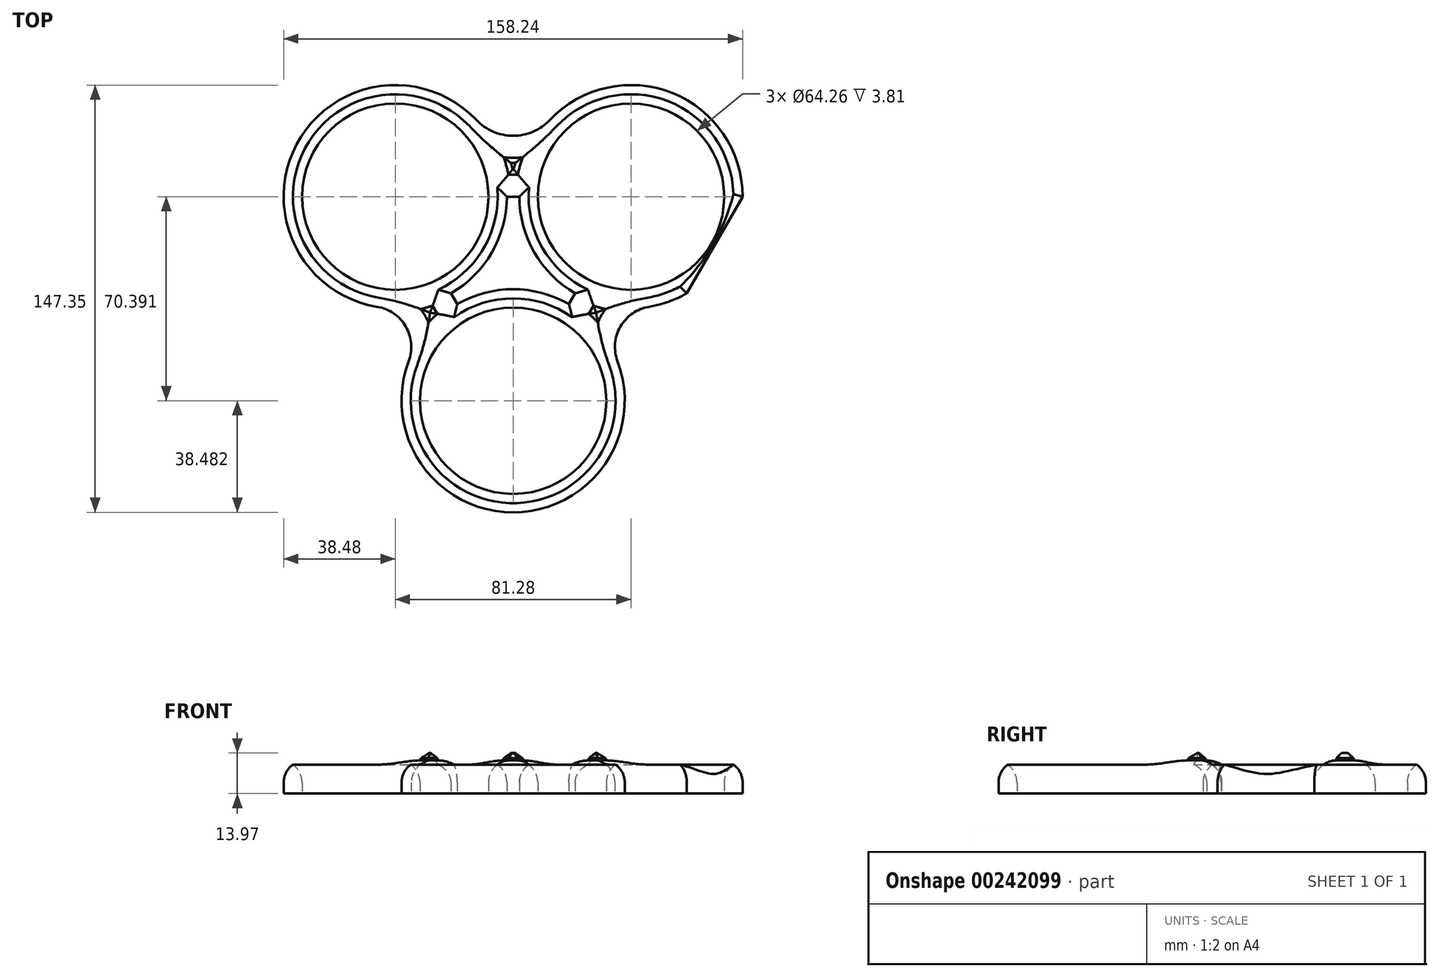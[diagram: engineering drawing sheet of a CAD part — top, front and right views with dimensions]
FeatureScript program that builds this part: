
annotation { "Feature Type Name" : "Feature", "Feature Type Description" : "" }
export const myFeature = defineFeature(function(context is Context, id is Id, definition is map)
    precondition{}
    {
        {
            var Q0;
            Q0=qCreatedBy(makeId("Top.planeOp"),FACE);
            var sketch = newSketch(context, id + "F0", { "sketchPlane" : qUnion([Q0])});
            skCircle(sketch, "E0", {"center": v(-40.64, 29.67) * mm, "radius": 32.13 * mm});
            skCircle(sketch, "E1", {"center": v(40.64, 29.67) * mm, "radius": 32.13 * mm});
            skCircle(sketch, "E2", {"center": v(0, -40.72) * mm, "radius": 32.13 * mm});
            skCircle(sketch, "E3", {"center": v(0, 0) * mm, "radius": 114.2 * mm});
            skCircle(sketch, "E4.0", {"center": v(-40.64, 29.67) * mm, "radius": 38.48 * mm});
            skCircle(sketch, "E5.0", {"center": v(40.64, 29.67) * mm, "radius": 38.48 * mm});
            skCircle(sketch, "E6.0", {"center": v(0, -40.72) * mm, "radius": 38.48 * mm});
            skLineSegment(sketch, "E7", {"start": v(-60.1, 96.9) * mm, "end": v(60.55, 96.9) * mm});
            skLineSegment(sketch, "E8", {"start": v(-79.12, 29.67) * mm, "end": v(-38.48, -40.72) * mm});
            skLineSegment(sketch, "E9", {"start": v(38.48, -40.72) * mm, "end": v(79.12, 29.67) * mm});
            skLineSegment(sketch, "E10", {"start": v(-40.64, 68.15) * mm, "end": v(40.64, 68.15) * mm});
            skLineSegment(sketch, "E11", {"start": v(-40.64, 29.67) * mm, "end": v(40.64, 29.67) * mm});
            skLineSegment(sketch, "E12", {"start": v(40.64, 29.67) * mm, "end": v(0, -40.72) * mm});
            skLineSegment(sketch, "E13", {"start": v(-40.64, 29.67) * mm, "end": v(0, -40.72) * mm});
            skLineSegment(sketch, "E14", {"start": v(-20.32, -5.52) * mm, "end": v(-49.18, -22.19) * mm});
            skLineSegment(sketch, "E15", {"start": v(20.32, -5.52) * mm, "end": v(49.18, -22.19) * mm});
            skLineSegment(sketch, "E16", {"start": v(0, 29.67) * mm, "end": v(0, 68.15) * mm});
            skCircle(sketch, "E17", {"center": v(49.18, -22.19) * mm, "radius": 14.08 * mm});
            skCircle(sketch, "E18", {"center": v(-49.18, -22.19) * mm, "radius": 14.08 * mm});
            skCircle(sketch, "E19", {"center": v(0, 68.15) * mm, "radius": 17.49 * mm});
            skSolve(sketch);
        }
        {
            var Q0;
            {var subQ5=sQuery(id+"F0.wireOp",EDGE,"E0");var subQ9=sQuery(id+"F0.wireOp",EDGE,"E11");var subQ11=makeQuery(id+"F0.imprint","INTERSECT",VERTEX,{"derivedFrom":[subQ5,subQ9]});Q0=makeQuery(id+"F0.imprint","IMPRINT",FACE,{"disambiguationData":[TD([[makeQuery(id+"F0.imprint","IMPRINT",EDGE,{"disambiguationData":[TD([[subQ11,-1.0]])],"derivedFrom":subQ5}),-1.0]])]});}
            var Q1;
            {var subQ8=sQuery(id+"F0.wireOp",EDGE,"E11");var subQ9=sQuery(id+"F0.wireOp",EDGE,"E1");var subQ10=makeQuery(id+"F0.imprint","INTERSECT",VERTEX,{"derivedFrom":[subQ9,subQ8]});Q1=makeQuery(id+"F0.imprint","IMPRINT",FACE,{"disambiguationData":[TD([[makeQuery(id+"F0.imprint","IMPRINT",EDGE,{"disambiguationData":[TD([[subQ10,1.0]])],"derivedFrom":subQ9}),-1.0]])]});}
            var Q2;
            {var subQ5=sQuery(id+"F0.wireOp",EDGE,"E12");var subQ8=sQuery(id+"F0.wireOp",EDGE,"E2");var subQ9=makeQuery(id+"F0.imprint","INTERSECT",VERTEX,{"derivedFrom":[subQ8,subQ5]});Q2=makeQuery(id+"F0.imprint","IMPRINT",FACE,{"disambiguationData":[TD([[makeQuery(id+"F0.imprint","IMPRINT",EDGE,{"disambiguationData":[TD([[subQ9,1.0]])],"derivedFrom":subQ8}),-1.0]])]});}
            var Q3;
            {var subQ0=sQuery(id+"F0.wireOp",EDGE,"E17");var subQ1=sQuery(id+"F0.wireOp",EDGE,"E6.0");var subQ2=makeQuery(id+"F0.imprint","INTERSECT",VERTEX,{"derivedFrom":[subQ1,subQ0]});Q3=makeQuery(id+"F0.imprint","IMPRINT",FACE,{"disambiguationData":[TD([[makeQuery(id+"F0.imprint","IMPRINT",EDGE,{"disambiguationData":[TD([[subQ2,-1.0]])],"derivedFrom":subQ1}),-1.0]])]});}
            var Q4;
            {var subQ0=sQuery(id+"F0.wireOp",EDGE,"E12");var subQ1=sQuery(id+"F0.wireOp",EDGE,"E5.0");var subQ2=makeQuery(id+"F0.imprint","INTERSECT",VERTEX,{"derivedFrom":[subQ1,subQ0]});Q4=makeQuery(id+"F0.imprint","IMPRINT",FACE,{"disambiguationData":[TD([[makeQuery(id+"F0.imprint","IMPRINT",EDGE,{"disambiguationData":[TD([[subQ2,-1.0]])],"derivedFrom":subQ1}),-1.0]])]});}
            var Q5;
            {var subQ0=sQuery(id+"F0.wireOp",EDGE,"E13");var subQ1=sQuery(id+"F0.wireOp",EDGE,"E6.0");var subQ2=makeQuery(id+"F0.imprint","INTERSECT",VERTEX,{"derivedFrom":[subQ1,subQ0]});Q5=makeQuery(id+"F0.imprint","IMPRINT",FACE,{"disambiguationData":[TD([[makeQuery(id+"F0.imprint","IMPRINT",EDGE,{"disambiguationData":[TD([[subQ2,-1.0]])],"derivedFrom":subQ1}),-1.0]])]});}
            var Q6;
            {var subQ0=sQuery(id+"F0.wireOp",EDGE,"E18");var subQ1=sQuery(id+"F0.wireOp",EDGE,"E4.0");var subQ2=makeQuery(id+"F0.imprint","INTERSECT",VERTEX,{"derivedFrom":[subQ1,subQ0]});Q6=makeQuery(id+"F0.imprint","IMPRINT",FACE,{"disambiguationData":[TD([[makeQuery(id+"F0.imprint","IMPRINT",EDGE,{"disambiguationData":[TD([[subQ2,-1.0]])],"derivedFrom":subQ1}),-1.0]])]});}
            var Q7;
            {var subQ0=sQuery(id+"F0.wireOp",EDGE,"E19");var subQ1=sQuery(id+"F0.wireOp",EDGE,"E4.0");var subQ2=makeQuery(id+"F0.imprint","INTERSECT",VERTEX,{"derivedFrom":[subQ1,subQ0]});Q7=makeQuery(id+"F0.imprint","IMPRINT",FACE,{"disambiguationData":[TD([[makeQuery(id+"F0.imprint","IMPRINT",EDGE,{"disambiguationData":[TD([[subQ2,1.0]])],"derivedFrom":subQ1}),-1.0]])]});}
            var Q8;
            {var subQ0=sQuery(id+"F0.wireOp",EDGE,"E19");var subQ1=sQuery(id+"F0.wireOp",EDGE,"E5.0");var subQ2=makeQuery(id+"F0.imprint","INTERSECT",VERTEX,{"derivedFrom":[subQ1,subQ0]});Q8=makeQuery(id+"F0.imprint","IMPRINT",FACE,{"disambiguationData":[TD([[makeQuery(id+"F0.imprint","IMPRINT",EDGE,{"disambiguationData":[TD([[subQ2,-1.0]])],"derivedFrom":subQ1}),-1.0]])]});}
            var Q9;
            {var subQ0=sQuery(id+"F0.wireOp",EDGE,"E11");var subQ1=sQuery(id+"F0.wireOp",EDGE,"E0");var subQ2=makeQuery(id+"F0.imprint","INTERSECT",VERTEX,{"derivedFrom":[subQ1,subQ0]});Q9=makeQuery(id+"F0.imprint","IMPRINT",FACE,{"disambiguationData":[TD([[makeQuery(id+"F0.imprint","IMPRINT",EDGE,{"disambiguationData":[TD([[subQ2,1.0]])],"derivedFrom":subQ1}),-1.0]])]});}
            var Q10;
            {var subQ0=sQuery(id+"F0.wireOp",EDGE,"E11");var subQ1=sQuery(id+"F0.wireOp",EDGE,"E1");var subQ2=makeQuery(id+"F0.imprint","INTERSECT",VERTEX,{"derivedFrom":[subQ1,subQ0]});Q10=makeQuery(id+"F0.imprint","IMPRINT",FACE,{"disambiguationData":[TD([[makeQuery(id+"F0.imprint","IMPRINT",EDGE,{"disambiguationData":[TD([[subQ2,-1.0]])],"derivedFrom":subQ1}),-1.0]])]});}
            var Q11;
            {var subQ0=sQuery(id+"F0.wireOp",EDGE,"E12");var subQ1=sQuery(id+"F0.wireOp",EDGE,"E2");var subQ2=makeQuery(id+"F0.imprint","INTERSECT",VERTEX,{"derivedFrom":[subQ1,subQ0]});Q11=makeQuery(id+"F0.imprint","IMPRINT",FACE,{"disambiguationData":[TD([[makeQuery(id+"F0.imprint","IMPRINT",EDGE,{"disambiguationData":[TD([[subQ2,-1.0]])],"derivedFrom":subQ1}),-1.0]])]});}
            var Q12;
            {var subQ0=sQuery(id+"F0.wireOp",EDGE,"E8");var subQ1=sQuery(id+"F0.wireOp",EDGE,"E4.0");var subQ2=makeQuery(id+"F0.imprint","INTERSECT",VERTEX,{"disambiguationData":[OD(0.0)],"derivedFrom":[subQ1,subQ0]});Q12=makeQuery(id+"F0.imprint","IMPRINT",FACE,{"disambiguationData":[TD([[makeQuery(id+"F0.imprint","IMPRINT",EDGE,{"disambiguationData":[TD([[subQ2,-1.0]])],"derivedFrom":subQ1}),1.0]])]});}
            var Q13;
            {var subQ0=sQuery(id+"F0.wireOp",EDGE,"E9");var subQ1=sQuery(id+"F0.wireOp",EDGE,"E5.0");var subQ2=makeQuery(id+"F0.imprint","INTERSECT",VERTEX,{"disambiguationData":[OD(0.0)],"derivedFrom":[subQ1,subQ0]});Q13=makeQuery(id+"F0.imprint","IMPRINT",FACE,{"disambiguationData":[TD([[makeQuery(id+"F0.imprint","IMPRINT",EDGE,{"disambiguationData":[TD([[subQ2,1.0]])],"derivedFrom":subQ1}),1.0]])]});}
            extrude(context, id + "F1", {"entities" : qUnion([Q0, Q1, Q2, Q3, Q4, Q5, Q6, Q7, Q8, Q9, Q10, Q11, Q12, Q13]), "depth" : 11.43 * mm});
        }
        {
            var Q0;
            Q0=makeQuery(id+"F1.opExtrude","CAP_FACE",FACE,{"disambiguationData":[OSD([sQuery(id+"F0.wireOp",EDGE,"E0"),sQuery(id+"F0.wireOp",EDGE,"E1"),sQuery(id+"F0.wireOp",EDGE,"E2"),sQuery(id+"F0.wireOp",EDGE,"E4.0"),sQuery(id+"F0.wireOp",EDGE,"E5.0"),sQuery(id+"F0.wireOp",EDGE,"E6.0"),sQuery(id+"F0.wireOp",EDGE,"E11"),sQuery(id+"F0.wireOp",EDGE,"E12"),sQuery(id+"F0.wireOp",EDGE,"E13"),sQuery(id+"F0.wireOp",EDGE,"E17"),sQuery(id+"F0.wireOp",EDGE,"E18"),sQuery(id+"F0.wireOp",EDGE,"E19")])],"isStart":false});
            fillet(context, id + "F2", {"entities" : qUnion([Q0]), "radius" : 7.62 * mm, "tangentPropagation" : true, "allowEdgeOverflow" : false});
        }
        {
            var Q0;
            Q0=makeQuery(id+"F2.opFillet","SPLIT",FACE,{"disambiguationData":[OD(2.0)],"derivedFrom":makeQuery(id+"F1.opExtrude","CAP_FACE",FACE,{"disambiguationData":[OSD([sQuery(id+"F0.wireOp",EDGE,"E0"),sQuery(id+"F0.wireOp",EDGE,"E1"),sQuery(id+"F0.wireOp",EDGE,"E2"),sQuery(id+"F0.wireOp",EDGE,"E4.0"),sQuery(id+"F0.wireOp",EDGE,"E5.0"),sQuery(id+"F0.wireOp",EDGE,"E6.0"),sQuery(id+"F0.wireOp",EDGE,"E11"),sQuery(id+"F0.wireOp",EDGE,"E12"),sQuery(id+"F0.wireOp",EDGE,"E13"),sQuery(id+"F0.wireOp",EDGE,"E17"),sQuery(id+"F0.wireOp",EDGE,"E18"),sQuery(id+"F0.wireOp",EDGE,"E19")])],"isStart":false})});
            var Q1;
            Q1=makeQuery(id+"F2.opFillet","SPLIT",FACE,{"disambiguationData":[OD(0.0)],"derivedFrom":makeQuery(id+"F1.opExtrude","CAP_FACE",FACE,{"disambiguationData":[OSD([sQuery(id+"F0.wireOp",EDGE,"E0"),sQuery(id+"F0.wireOp",EDGE,"E1"),sQuery(id+"F0.wireOp",EDGE,"E2"),sQuery(id+"F0.wireOp",EDGE,"E4.0"),sQuery(id+"F0.wireOp",EDGE,"E5.0"),sQuery(id+"F0.wireOp",EDGE,"E6.0"),sQuery(id+"F0.wireOp",EDGE,"E11"),sQuery(id+"F0.wireOp",EDGE,"E12"),sQuery(id+"F0.wireOp",EDGE,"E13"),sQuery(id+"F0.wireOp",EDGE,"E17"),sQuery(id+"F0.wireOp",EDGE,"E18"),sQuery(id+"F0.wireOp",EDGE,"E19")])],"isStart":false})});
            var Q2;
            Q2=makeQuery(id+"F2.opFillet","SPLIT",FACE,{"disambiguationData":[OD(1.0)],"derivedFrom":makeQuery(id+"F1.opExtrude","CAP_FACE",FACE,{"disambiguationData":[OSD([sQuery(id+"F0.wireOp",EDGE,"E0"),sQuery(id+"F0.wireOp",EDGE,"E1"),sQuery(id+"F0.wireOp",EDGE,"E2"),sQuery(id+"F0.wireOp",EDGE,"E4.0"),sQuery(id+"F0.wireOp",EDGE,"E5.0"),sQuery(id+"F0.wireOp",EDGE,"E6.0"),sQuery(id+"F0.wireOp",EDGE,"E11"),sQuery(id+"F0.wireOp",EDGE,"E12"),sQuery(id+"F0.wireOp",EDGE,"E13"),sQuery(id+"F0.wireOp",EDGE,"E17"),sQuery(id+"F0.wireOp",EDGE,"E18"),sQuery(id+"F0.wireOp",EDGE,"E19")])],"isStart":false})});
            extrude(context, id + "F3", {"entities" : qUnion([Q0, Q1, Q2]), "operationType" : NewBodyOperationType.ADD, "depth" : 2.54 * mm});
        }
        {
            var Q0;
            {var subQ0=sQuery(id+"F0.wireOp",EDGE,"E19");var subQ1=sQuery(id+"F0.wireOp",EDGE,"E18");var subQ2=sQuery(id+"F0.wireOp",EDGE,"E17");var subQ3=sQuery(id+"F0.wireOp",EDGE,"E13");var subQ4=sQuery(id+"F0.wireOp",EDGE,"E12");var subQ5=sQuery(id+"F0.wireOp",EDGE,"E11");var subQ6=sQuery(id+"F0.wireOp",EDGE,"E6.0");var subQ7=sQuery(id+"F0.wireOp",EDGE,"E5.0");var subQ8=sQuery(id+"F0.wireOp",EDGE,"E4.0");var subQ9=sQuery(id+"F0.wireOp",EDGE,"E2");var subQ10=sQuery(id+"F0.wireOp",EDGE,"E1");var subQ11=sQuery(id+"F0.wireOp",EDGE,"E0");Q0=makeQuery(id+"F3.opExtrude","CAP_FACE",FACE,{"disambiguationData":[OSD([subQ11,subQ10,subQ9,subQ8,subQ7,subQ6,subQ5,subQ4,subQ3,subQ2,subQ1,subQ0]),TDD([makeQuery(id+"F2.opFillet","SPLIT",FACE,{"disambiguationData":[OD(2.0)],"derivedFrom":makeQuery(id+"F1.opExtrude","CAP_FACE",FACE,{"disambiguationData":[OSD([subQ11,subQ10,subQ9,subQ8,subQ7,subQ6,subQ5,subQ4,subQ3,subQ2,subQ1,subQ0])],"isStart":false})})])],"isStart":false});}
            var Q1;
            {var subQ0=sQuery(id+"F0.wireOp",EDGE,"E19");var subQ1=sQuery(id+"F0.wireOp",EDGE,"E18");var subQ2=sQuery(id+"F0.wireOp",EDGE,"E17");var subQ3=sQuery(id+"F0.wireOp",EDGE,"E13");var subQ4=sQuery(id+"F0.wireOp",EDGE,"E12");var subQ5=sQuery(id+"F0.wireOp",EDGE,"E11");var subQ6=sQuery(id+"F0.wireOp",EDGE,"E6.0");var subQ7=sQuery(id+"F0.wireOp",EDGE,"E5.0");var subQ8=sQuery(id+"F0.wireOp",EDGE,"E4.0");var subQ9=sQuery(id+"F0.wireOp",EDGE,"E2");var subQ10=sQuery(id+"F0.wireOp",EDGE,"E1");var subQ11=sQuery(id+"F0.wireOp",EDGE,"E0");Q1=makeQuery(id+"F3.opExtrude","CAP_FACE",FACE,{"disambiguationData":[OSD([subQ11,subQ10,subQ9,subQ8,subQ7,subQ6,subQ5,subQ4,subQ3,subQ2,subQ1,subQ0]),TDD([makeQuery(id+"F2.opFillet","SPLIT",FACE,{"disambiguationData":[OD(0.0)],"derivedFrom":makeQuery(id+"F1.opExtrude","CAP_FACE",FACE,{"disambiguationData":[OSD([subQ11,subQ10,subQ9,subQ8,subQ7,subQ6,subQ5,subQ4,subQ3,subQ2,subQ1,subQ0])],"isStart":false})})])],"isStart":false});}
            var Q2;
            {var subQ0=sQuery(id+"F0.wireOp",EDGE,"E19");var subQ1=sQuery(id+"F0.wireOp",EDGE,"E18");var subQ2=sQuery(id+"F0.wireOp",EDGE,"E17");var subQ3=sQuery(id+"F0.wireOp",EDGE,"E13");var subQ4=sQuery(id+"F0.wireOp",EDGE,"E12");var subQ5=sQuery(id+"F0.wireOp",EDGE,"E11");var subQ6=sQuery(id+"F0.wireOp",EDGE,"E6.0");var subQ7=sQuery(id+"F0.wireOp",EDGE,"E5.0");var subQ8=sQuery(id+"F0.wireOp",EDGE,"E4.0");var subQ9=sQuery(id+"F0.wireOp",EDGE,"E2");var subQ10=sQuery(id+"F0.wireOp",EDGE,"E1");var subQ11=sQuery(id+"F0.wireOp",EDGE,"E0");Q2=makeQuery(id+"F3.opExtrude","CAP_FACE",FACE,{"disambiguationData":[OSD([subQ11,subQ10,subQ9,subQ8,subQ7,subQ6,subQ5,subQ4,subQ3,subQ2,subQ1,subQ0]),TDD([makeQuery(id+"F2.opFillet","SPLIT",FACE,{"disambiguationData":[OD(1.0)],"derivedFrom":makeQuery(id+"F1.opExtrude","CAP_FACE",FACE,{"disambiguationData":[OSD([subQ11,subQ10,subQ9,subQ8,subQ7,subQ6,subQ5,subQ4,subQ3,subQ2,subQ1,subQ0])],"isStart":false})})])],"isStart":false});}
            chamfer(context, id + "F4", {"entities" : qUnion([Q0, Q1, Q2]), "width" : 1.78 * mm, "tangentPropagation" : true});
        }
    });
